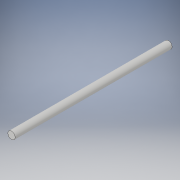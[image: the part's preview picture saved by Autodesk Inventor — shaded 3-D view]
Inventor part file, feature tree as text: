
AUTODESK INVENTOR PART (.ipt)
format: ipt  version: 2019 (Build 230136000, 136)  size: 90,112 bytes
history: native  units: mm
features: extrude x1, sketch x1
ambient origin geometry x8: Origin, YZ Plane, XZ Plane, XY Plane, X Axis, Y Axis, Z Axis, Center Point
bodies: Solid1 (feature_tree)
feature tree (2):
  extrude  "Extrusion1"  Depth=150.0mm TaperAngle=0.0deg
  sketch  "Sketch1"  dims[d0=7.0mm d1=150.0mm d2=0.0mm]
